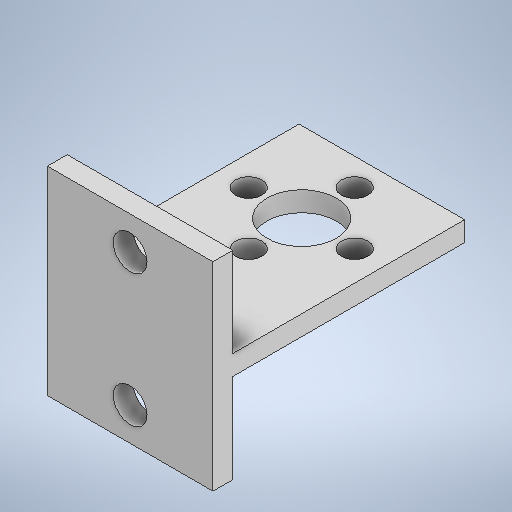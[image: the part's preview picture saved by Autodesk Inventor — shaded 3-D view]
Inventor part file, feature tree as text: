
AUTODESK INVENTOR PART (.ipt)
format: ipt  version: 2025.2 (Build 292293000, 293)  size: 253,952 bytes
history: native  units: mm
features: sketch x5, extrude x4
ambient origin geometry x8: Origin, YZ Plane, XZ Plane, XY Plane, X Axis, Y Axis, Z Axis, Center Point
bodies: Solid1 (feature_tree)
feature tree (9):
  extrude  "Extrusion1"  Depth=30.0mm
  extrude  "Extrusion2"  Depth=3.0mm
  extrude  "Extrusion3"  Depth=35.0mm
  extrude  "Extrusion4"  Depth=5.1mm
  sketch  "Sketch1"  dims[d0=25.0mm d1=30.0mm]
  sketch  "Sketch2"  dims[d5=35.0mm d6=0.0mm d7=20.0mm]
  sketch  "Sketch3"  dims[d8=5.1mm d9=5.1mm]
  sketch  "Sketch4"  dims[d10=0.0mm d11=0.0mm d12=22.896mm d13=10.5mm d14=16.0mm d15=4.0mm d16=40.0mm d18=360.0deg d20=0.0mm d21=0.0mm]
  sketch  "Sketch Circular Pattern1"  dims[d2=3.0mm d3=0.0mm d4=3.0mm]
